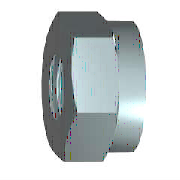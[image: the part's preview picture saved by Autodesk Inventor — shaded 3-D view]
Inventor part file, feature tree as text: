
AUTODESK INVENTOR PART (.ipt)
format: ipt  version: 2025 (Build 290162010, 162A)  size: 178,688 bytes
history: native  units: mm (DEFAULTED — no unit token found)
features: extrude x1, chamfer x1, hole x1, other x1, plane x1
ambient origin geometry x7: Origin, YZ Plane, XZ Plane, X Axis, Y Axis, Z Axis, Center Point
bodies: Solid1 (feature_tree), Body (feature_tree)
feature tree (5):
  extrude  "Ring"  Depth=6.350853mm
  chamfer  "Chamfer1"  Distance=1.55mm
  hole  "Thread"  [1 undecoded]
  other  "Work Axis1"
  plane  "Work Plane1"
note: 1 required parameter value undecoded (feature->parameter linkage not recoverable at this tier; creation-order binding heuristic only, values carry confidence <= 0.55)
